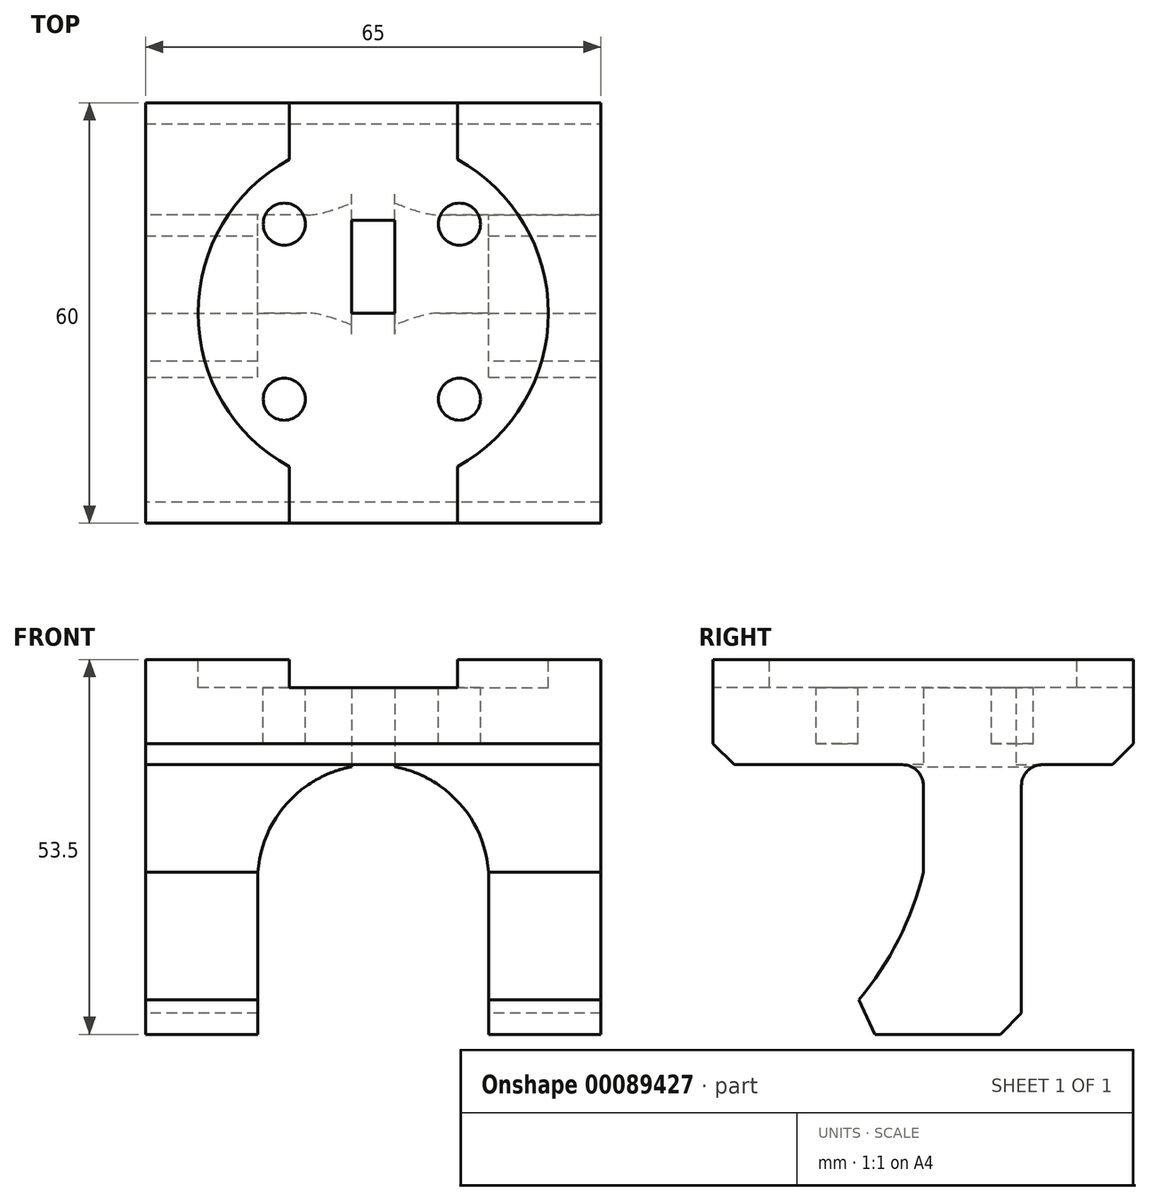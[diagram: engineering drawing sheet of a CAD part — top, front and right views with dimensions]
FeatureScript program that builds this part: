
annotation { "Feature Type Name" : "Feature", "Feature Type Description" : "" }
export const myFeature = defineFeature(function(context is Context, id is Id, definition is map)
    precondition{}
    {
        {
            var Q0;
            Q0=qCreatedBy(makeId("Top.planeOp"),FACE);
            var sketch = newSketch(context, id + "F0", { "sketchPlane" : qUnion([Q0])});
            skLineSegment(sketch, "E0.bottom", {"start": v(32.5, 30) * mm, "end": v(-32.5, 30) * mm});
            skLineSegment(sketch, "E0.top", {"start": v(32.5, -30) * mm, "end": v(-32.5, -30) * mm});
            skLineSegment(sketch, "E0.left", {"start": v(32.5, 30) * mm, "end": v(32.5, -30) * mm});
            skLineSegment(sketch, "E0.right", {"start": v(-32.5, 30) * mm, "end": v(-32.5, -30) * mm});
            skPoint(sketch, "E1.middle", {"position": v(0, 0) * mm});
            skLineSegment(sketch, "E2.bottom", {"start": v(3.07, 0) * mm, "end": v(-3.08, 0) * mm});
            skLineSegment(sketch, "E2.top", {"start": v(3.07, 13.25) * mm, "end": v(-3.08, 13.25) * mm});
            skLineSegment(sketch, "E2.left", {"start": v(3.07, 0) * mm, "end": v(3.08, 13.25) * mm});
            skLineSegment(sketch, "E2.right", {"start": v(-3.08, 0) * mm, "end": v(-3.08, 13.25) * mm});
            skPoint(sketch, "E2.middle", {"position": v(0, 6.62) * mm});
            skPoint(sketch, "E3", {"position": v(0, -30) * mm});
            skSolve(sketch);
        }
        {
            var Q0;
            Q0=makeQuery(id+"F0.imprint","IMPRINT",FACE,{"disambiguationData":[TD([[makeQuery(id+"F0.imprint","IMPRINT",EDGE,{"derivedFrom":sQuery(id+"F0.wireOp",EDGE,"E0.bottom")}),1.0]])]});
            extrude(context, id + "F1", {"entities" : qUnion([Q0]), "depth" : 15 * mm});
        }
        {
            var Q0;
            Q0=qCreatedBy(makeId("Front.planeOp"),FACE);
            var sketch = newSketch(context, id + "F2", { "sketchPlane" : qUnion([Q0])});
            skLineSegment(sketch, "E4", {"start": v(-32.5, 0) * mm, "end": v(-32.5, -38.5) * mm});
            skLineSegment(sketch, "E5", {"start": v(-16.5, -16.5) * mm, "end": v(-16.5, -38.5) * mm});
            skLineSegment(sketch, "E6", {"start": v(-16.5, -38.5) * mm, "end": v(-32.5, -38.5) * mm});
            skArc(sketch, "E7", {"start": v(-3.07, -0.29) * mm, "mid": v(-12.7, -5.98) * mm, "end": v(-16.5, -16.5) * mm});
            skLineSegment(sketch, "E8", {"start": v(-3.08, 0) * mm, "end": v(3.08, 0) * mm, "construction": true});
            skLineSegment(sketch, "E9", {"start": v(-3.08, 0) * mm, "end": v(-3.08, -0.29) * mm});
            skLineSegment(sketch, "E10", {"start": v(-3.07, 0) * mm, "end": v(-32.5, 0) * mm});
            skPoint(sketch, "E11.orphan", {"position": v(0, 0) * mm});
            skArc(sketch, "E12.MirrorCS", {"start": v(3.07, -0.29) * mm, "mid": v(12.7, -5.98) * mm, "end": v(16.5, -16.5) * mm});
            skLineSegment(sketch, "E13.MirrorCS", {"start": v(3.08, 0) * mm, "end": v(3.08, -0.29) * mm});
            skLineSegment(sketch, "E14.MirrorCS", {"start": v(3.07, 0) * mm, "end": v(32.5, 0) * mm});
            skLineSegment(sketch, "E15.MirrorCS", {"start": v(32.5, 0) * mm, "end": v(32.5, -38.5) * mm});
            skLineSegment(sketch, "E16.MirrorCS", {"start": v(16.5, -38.5) * mm, "end": v(32.5, -38.5) * mm});
            skLineSegment(sketch, "E17.MirrorCS", {"start": v(16.5, -16.5) * mm, "end": v(16.5, -38.5) * mm});
            skSolve(sketch);
        }
        {
            var Q0;
            Q0 = qSketchRegion(id + "F2", true);
            extrude(context, id + "F3", {"entities" : qUnion([Q0]), "operationType" : NewBodyOperationType.ADD, "endBound" : BoundingType.SYMMETRIC, "depth" : 28 * mm});
        }
        {
            var Q0;
            Q0=makeQuery(id+"F1.opExtrude","CAP_FACE",FACE,{"disambiguationData":[OSD([sQuery(id+"F0.wireOp",EDGE,"E0.bottom"),sQuery(id+"F0.wireOp",EDGE,"E0.top"),sQuery(id+"F0.wireOp",EDGE,"E0.left"),sQuery(id+"F0.wireOp",EDGE,"E0.right"),sQuery(id+"F0.wireOp",EDGE,"E1.bottom"),sQuery(id+"F0.wireOp",EDGE,"E1.top"),sQuery(id+"F0.wireOp",EDGE,"E1.left"),sQuery(id+"F0.wireOp",EDGE,"E1.right"),sQuery(id+"F0.wireOp",EDGE,"JrXA6PBr-tPex-jOhf-22ll-jyP1Bfv6VaY5.bottom"),sQuery(id+"F0.wireOp",EDGE,"JrXA6PBr-tPex-jOhf-22ll-jyP1Bfv6VaY5.top"),sQuery(id+"F0.wireOp",EDGE,"JrXA6PBr-tPex-jOhf-22ll-jyP1Bfv6VaY5.left"),sQuery(id+"F0.wireOp",EDGE,"JrXA6PBr-tPex-jOhf-22ll-jyP1Bfv6VaY5.right")])],"isStart":false});
            var sketch = newSketch(context, id + "F4", { "sketchPlane" : qUnion([Q0])});
            skCircle(sketch, "E18", {"center": v(0, 0) * mm, "radius": 25 * mm, "construction": true});
            skLineSegment(sketch, "E19", {"start": v(12, 21.93) * mm, "end": v(12, 35) * mm});
            skLineSegment(sketch, "E20", {"start": v(12, 35) * mm, "end": v(-12, 35) * mm});
            skLineSegment(sketch, "E21", {"start": v(-12, 35) * mm, "end": v(-12, 21.93) * mm});
            skLineSegment(sketch, "E22", {"start": v(-12, -21.93) * mm, "end": v(-12, -35) * mm});
            skLineSegment(sketch, "E23", {"start": v(-12, -35) * mm, "end": v(12, -35) * mm});
            skLineSegment(sketch, "E24", {"start": v(12, -35) * mm, "end": v(12, -21.93) * mm});
            skArc(sketch, "E25", {"start": v(-12, 21.93) * mm, "mid": v(-25, 0) * mm, "end": v(-12, -21.93) * mm});
            skArc(sketch, "E26", {"start": v(12, 21.93) * mm, "mid": v(25, 0) * mm, "end": v(12, -21.93) * mm});
            skSolve(sketch);
        }
        {
            var Q0;
            Q0 = qSketchRegion(id + "F4", true);
            extrude(context, id + "F5", {"entities" : qUnion([Q0]), "operationType" : NewBodyOperationType.REMOVE, "oppositeDirection" : true, "depth" : 4 * mm});
        }
        {
            var Q0;
            Q0=makeQuery(id+"F5.boolean.opBoolean","COPY",FACE,{"derivedFrom":makeQuery(id+"F5.opExtrude","CAP_FACE",FACE,{"disambiguationData":[OSD([sQuery(id+"F4.wireOp",EDGE,"E19"),sQuery(id+"F4.wireOp",EDGE,"E20"),sQuery(id+"F4.wireOp",EDGE,"E21"),sQuery(id+"F4.wireOp",EDGE,"E22"),sQuery(id+"F4.wireOp",EDGE,"E23"),sQuery(id+"F4.wireOp",EDGE,"E24"),sQuery(id+"F4.wireOp",EDGE,"E25"),sQuery(id+"F4.wireOp",EDGE,"E26")])],"isStart":false})});
            var sketch = newSketch(context, id + "F6", { "sketchPlane" : qUnion([Q0])});
            skCircle(sketch, "E27", {"center": v(-12.7, 12.7) * mm, "radius": 3 * mm});
            skCircle(sketch, "E28.0.1.0", {"center": v(-12.7, -12.3) * mm, "radius": 3 * mm});
            skCircle(sketch, "E28.1.0.0", {"center": v(12.3, 12.7) * mm, "radius": 3 * mm});
            skCircle(sketch, "E28.1.1.0", {"center": v(12.3, -12.3) * mm, "radius": 3 * mm});
            skLineSegment(sketch, "E28.direction1", {"start": v(-12.7, 12.7) * mm, "end": v(12.3, 12.7) * mm, "construction": true});
            skLineSegment(sketch, "E28.direction2", {"start": v(-12.7, 12.7) * mm, "end": v(-12.7, -12.3) * mm, "construction": true});
            skSolve(sketch);
        }
        {
            var Q0;
            Q0=makeQuery(id+"F6.imprint","IMPRINT",FACE,{"disambiguationData":[TD([[makeQuery(id+"F6.imprint","IMPRINT",EDGE,{"derivedFrom":sQuery(id+"F6.wireOp",EDGE,"E27")}),1.0]])]});
            var Q1;
            Q1=makeQuery(id+"F6.imprint","IMPRINT",FACE,{"disambiguationData":[TD([[makeQuery(id+"F6.imprint","IMPRINT",EDGE,{"derivedFrom":sQuery(id+"F6.wireOp",EDGE,"E28.1.0.0")}),1.0]])]});
            var Q2;
            Q2=makeQuery(id+"F6.imprint","IMPRINT",FACE,{"disambiguationData":[TD([[makeQuery(id+"F6.imprint","IMPRINT",EDGE,{"derivedFrom":sQuery(id+"F6.wireOp",EDGE,"E28.1.1.0")}),1.0]])]});
            var Q3;
            Q3=makeQuery(id+"F6.imprint","IMPRINT",FACE,{"disambiguationData":[TD([[makeQuery(id+"F6.imprint","IMPRINT",EDGE,{"derivedFrom":sQuery(id+"F6.wireOp",EDGE,"E28.0.1.0")}),1.0]])]});
            extrude(context, id + "F7", {"entities" : qUnion([Q0, Q1, Q2, Q3]), "operationType" : NewBodyOperationType.REMOVE, "oppositeDirection" : true, "depth" : 8 * mm});
        }
        {
            var Q0;
            Q0=makeQuery(id+"F3.boolean.opBoolean","MERGE",FACE,{"derivedFrom":[makeQuery(id+"F1.opExtrude","SWEPT_FACE",FACE,{"disambiguationData":[OSD([sQuery(id+"F0.wireOp",EDGE,"E0.left")])]}),makeQuery(id+"F3.opExtrude","SWEPT_FACE",FACE,{"disambiguationData":[OSD([sQuery(id+"F2.wireOp",EDGE,"E15.MirrorCS")])]})]});
            var sketch = newSketch(context, id + "F8", { "sketchPlane" : qUnion([Q0])});
            skLineSegment(sketch, "E29", {"start": v(0, 0) * mm, "end": v(0, -15.38) * mm});
            skLineSegment(sketch, "E30", {"start": v(-14, -38.5) * mm, "end": v(-14, 0) * mm});
            skLineSegment(sketch, "E31", {"start": v(-14, 0) * mm, "end": v(0, 0) * mm});
            skArc(sketch, "E32", {"start": v(-14, -38.5) * mm, "mid": v(-5.22, -28.01) * mm, "end": v(0, -15.38) * mm});
            skSolve(sketch);
        }
        {
            var Q0;
            Q0 = qSketchRegion(id + "F8", true);
            extrude(context, id + "F9", {"entities" : qUnion([Q0]), "operationType" : NewBodyOperationType.REMOVE, "oppositeDirection" : true, "depth" : 90 * mm});
        }
        {
            var Q0;
            Q0=makeQuery(id+"F9.boolean.opBoolean","COPY",EDGE,{"disambiguationData":[OD(1.0)],"derivedFrom":makeQuery(id+"F9.opExtrude","SWEPT_EDGE",EDGE,{"disambiguationData":[OSD([sQuery(id+"F8.wireOp",EDGE,"E29"),sQuery(id+"F8.wireOp",EDGE,"E31")])]})});
            var Q1;
            Q1=makeQuery(id+"F9.boolean.opBoolean","COPY",EDGE,{"disambiguationData":[OD(0.0)],"derivedFrom":makeQuery(id+"F9.opExtrude","SWEPT_EDGE",EDGE,{"disambiguationData":[OSD([sQuery(id+"F8.wireOp",EDGE,"E29"),sQuery(id+"F8.wireOp",EDGE,"E31")])]})});
            var Q2;
            Q2=makeQuery(id+"F3.opExtrude","CAP_EDGE",EDGE,{"disambiguationData":[OSD([sQuery(id+"F2.wireOp",EDGE,"E10")])],"isStart":true});
            var Q3;
            Q3=makeQuery(id+"F3.opExtrude","CAP_EDGE",EDGE,{"disambiguationData":[OSD([sQuery(id+"F2.wireOp",EDGE,"E14.MirrorCS")])],"isStart":true});
            fillet(context, id + "F10", {"entities" : qUnion([Q0, Q1, Q2, Q3]), "radius" : 3 * mm, "tangentPropagation" : true, "allowEdgeOverflow" : false});
        }
        {
            var Q0;
            Q0=makeQuery(id+"F1.opExtrude","CAP_EDGE",EDGE,{"disambiguationData":[OSD([sQuery(id+"F0.wireOp",EDGE,"E0.top")])],"isStart":true});
            var Q1;
            Q1=makeQuery(id+"F1.opExtrude","CAP_EDGE",EDGE,{"disambiguationData":[OSD([sQuery(id+"F0.wireOp",EDGE,"E0.bottom")])],"isStart":true});
            var Q2;
            Q2=makeQuery(id+"F3.opExtrude","CAP_EDGE",EDGE,{"disambiguationData":[OSD([sQuery(id+"F2.wireOp",EDGE,"E6")])],"isStart":false});
            var Q3;
            Q3=makeQuery(id+"F3.opExtrude","CAP_EDGE",EDGE,{"disambiguationData":[OSD([sQuery(id+"F2.wireOp",EDGE,"E16.MirrorCS")])],"isStart":false});
            var Q4;
            Q4=makeQuery(id+"F3.opExtrude","CAP_EDGE",EDGE,{"disambiguationData":[OSD([sQuery(id+"F2.wireOp",EDGE,"E16.MirrorCS")])],"isStart":true});
            var Q5;
            Q5=makeQuery(id+"F3.opExtrude","CAP_EDGE",EDGE,{"disambiguationData":[OSD([sQuery(id+"F2.wireOp",EDGE,"E6")])],"isStart":true});
            chamfer(context, id + "F11", {"entities" : qUnion([Q0, Q1, Q2, Q3, Q4, Q5]), "width" : 3 * mm, "tangentPropagation" : true});
        }
    });
